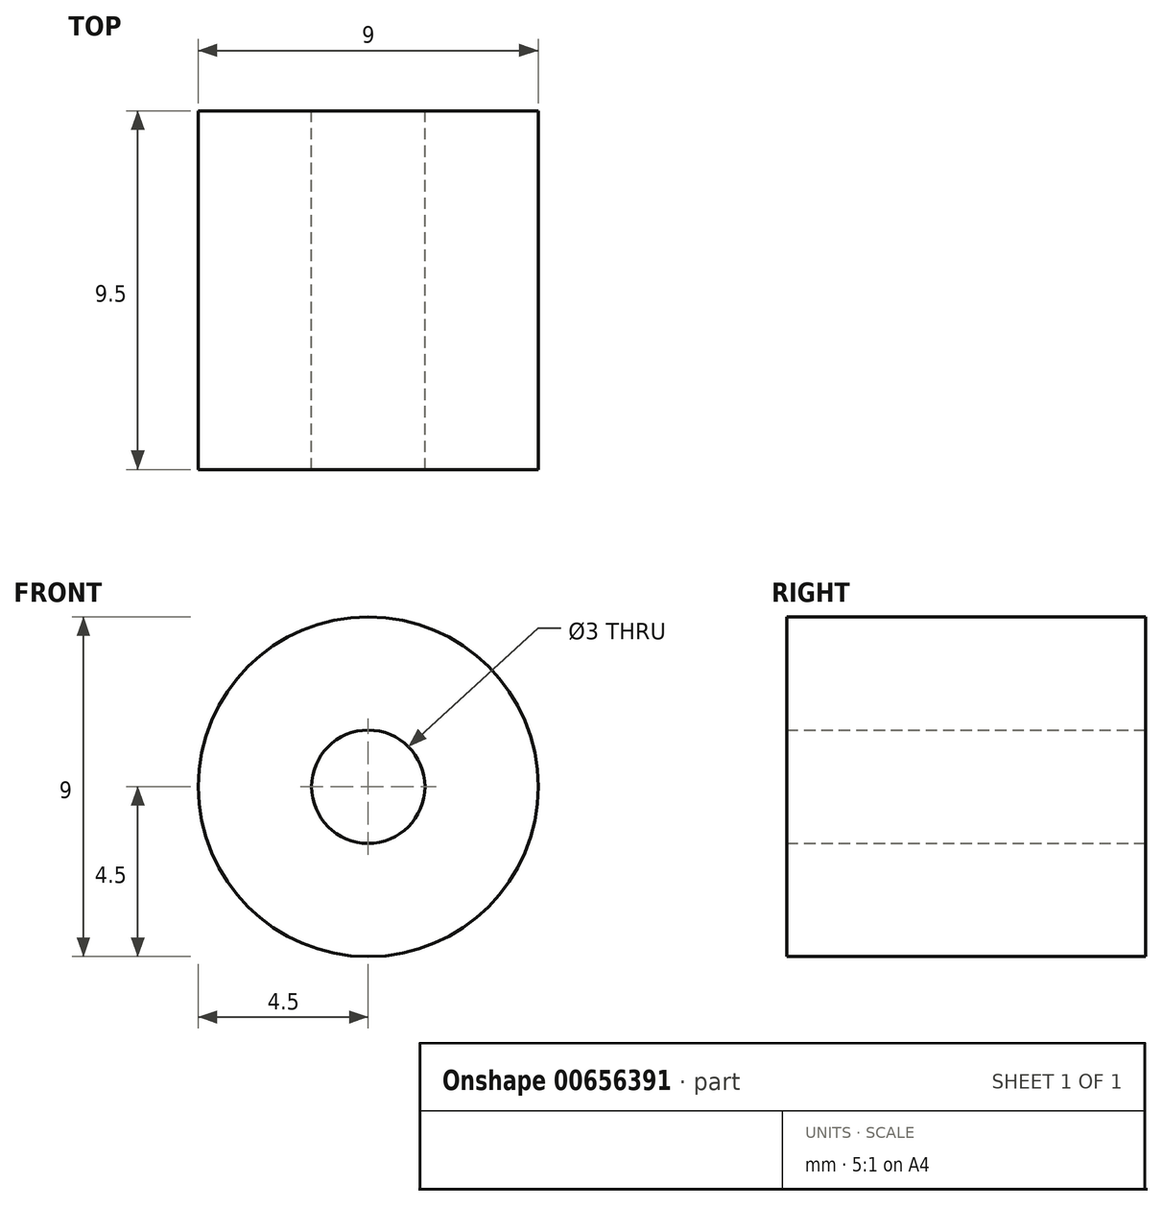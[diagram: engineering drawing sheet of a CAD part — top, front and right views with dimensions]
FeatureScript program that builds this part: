
annotation { "Feature Type Name" : "Feature", "Feature Type Description" : "" }
export const myFeature = defineFeature(function(context is Context, id is Id, definition is map)
    precondition{}
    {
        {
            var Q0;
            Q0=qCreatedBy(makeId("Front.planeOp"),FACE);
            var sketch = newSketch(context, id + "F0", { "sketchPlane" : qUnion([Q0])});
            skCircle(sketch, "E0", {"center": v(0, 0) * mm, "radius": 4.5 * mm});
            skCircle(sketch, "E1", {"center": v(0, 0) * mm, "radius": 1.5 * mm});
            skSolve(sketch);
        }
        {
            var Q0;
            Q0=makeQuery(id+"F0.imprint","IMPRINT",FACE,{"disambiguationData":[TD([[makeQuery(id+"F0.imprint","IMPRINT",EDGE,{"derivedFrom":sQuery(id+"F0.wireOp",EDGE,"E0")}),1.0]])]});
            extrude(context, id + "F1", {"entities" : qUnion([Q0]), "depth" : 9.5 * mm, "offsetDistance" : 25 * mm});
        }
    });
